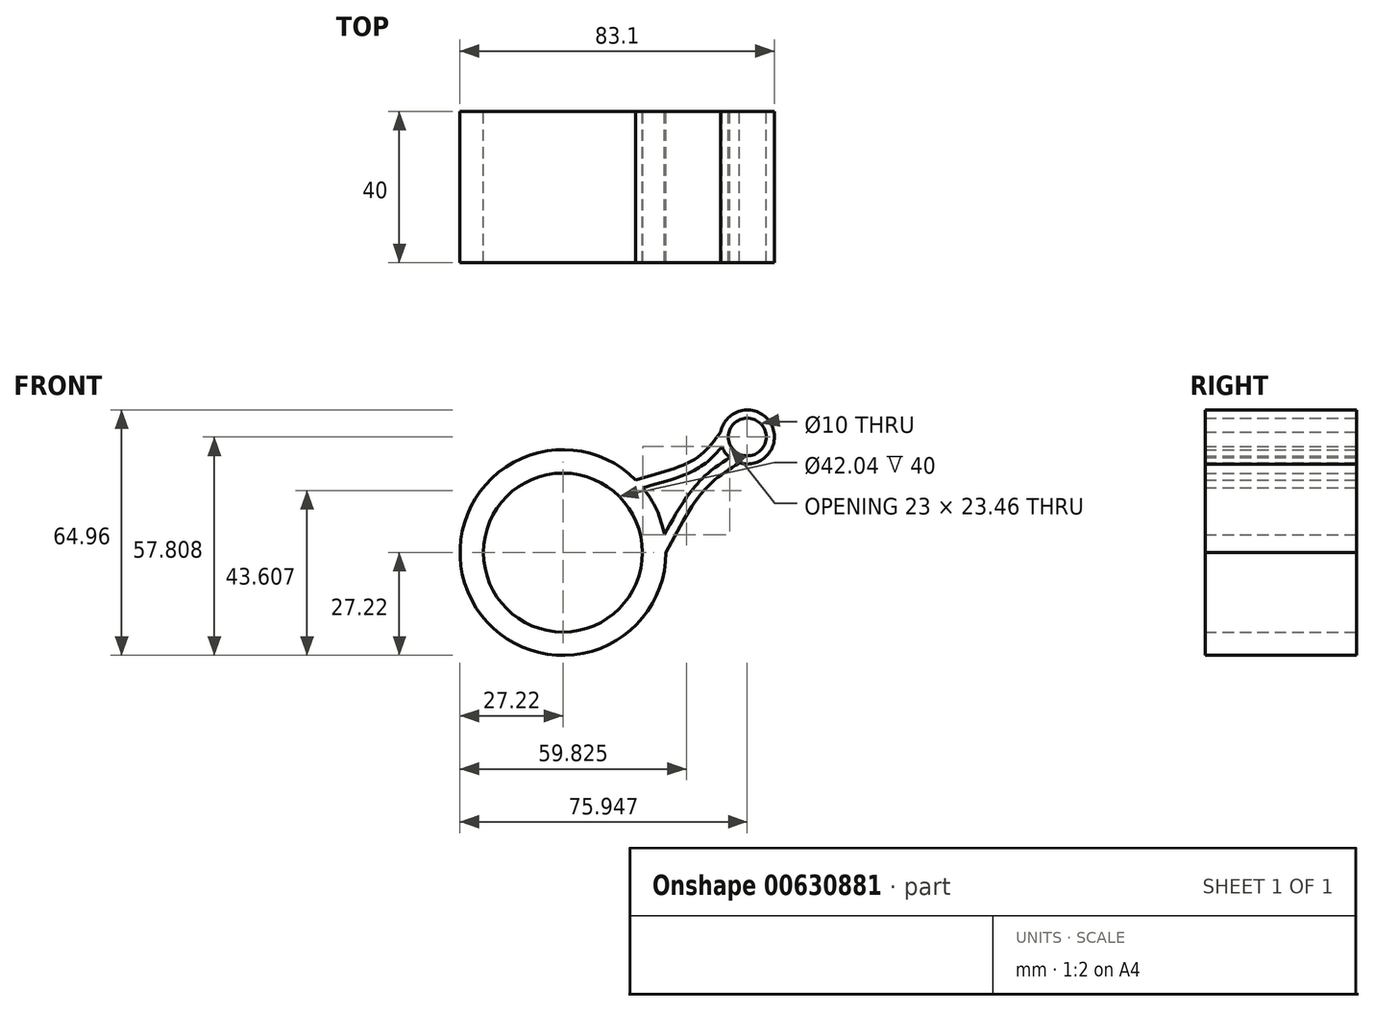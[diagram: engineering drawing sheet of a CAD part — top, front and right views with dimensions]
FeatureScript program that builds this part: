
annotation { "Feature Type Name" : "Feature", "Feature Type Description" : "" }
export const myFeature = defineFeature(function(context is Context, id is Id, definition is map)
    precondition{}
    {
        {
            var Q0;
            Q0=qCreatedBy(makeId("Front.planeOp"),FACE);
            var sketch = newSketch(context, id + "F0", { "sketchPlane" : qUnion([Q0])});
            skCircle(sketch, "E0", {"center": v(0, 0) * mm, "radius": 27.22 * mm});
            skLineSegment(sketch, "E1", {"start": v(0, 0) * mm, "end": v(0, 27.22) * mm});
            skLineSegment(sketch, "E2", {"start": v(0, 27.22) * mm, "end": v(0, 0) * mm});
            skLineSegment(sketch, "E3", {"start": v(27.22, 0) * mm, "end": v(0, 0) * mm});
            skLineSegment(sketch, "E4", {"start": v(0, 0) * mm, "end": v(19.24, 19.24) * mm});
            skCircle(sketch, "E5", {"center": v(0, 0) * mm, "radius": 21.02 * mm});
            skFitSpline(sketch, "E6", {"points": [v(27.22, 0) * mm, v(37.3, 16.46) * mm, v(46.6, 23.76) * mm], "startDerivative": vector(17.1, 32.9) * mm, "endDerivative": vector(21.89, 13.84) * mm});
            skFitSpline(sketch, "E7", {"points": [v(19.24, 19.24) * mm, v(34.77, 24.69) * mm, v(41.76, 31.96) * mm], "startDerivative": vector(29, 8.4) * mm, "endDerivative": vector(14.79, 19.6) * mm});
            skCircle(sketch, "E8", {"center": v(48.73, 30.59) * mm, "radius": 7.15 * mm});
            skCircle(sketch, "E9", {"center": v(48.73, 30.59) * mm, "radius": 5 * mm});
            skFitSpline(sketch, "E10.0", {"points": [v(19.94, 16.84) * mm, v(21.13, 17.19) * mm, v(23.6, 17.87) * mm, v(27.42, 18.96) * mm, v(30.52, 19.97) * mm, v(32.88, 20.9) * mm, v(34.28, 21.56) * mm, v(35.35, 22.12) * mm, v(36.13, 22.58) * mm, v(36.87, 23.06) * mm, v(37.8, 23.73) * mm, v(38.85, 24.61) * mm, v(40.36, 26.1) * mm, v(41.97, 28.05) * mm, v(43.15, 29.65) * mm, v(43.75, 30.45) * mm]});
            skFitSpline(sketch, "E11.0", {"points": [v(25, 1.15) * mm, v(25.7, 2.52) * mm, v(27.14, 5.28) * mm, v(29.35, 9.33) * mm, v(31.27, 12.52) * mm, v(32.88, 14.91) * mm, v(33.93, 16.32) * mm, v(34.8, 17.4) * mm, v(35.7, 18.42) * mm, v(36.84, 19.62) * mm, v(38.24, 20.9) * mm, v(40.13, 22.45) * mm, v(42.5, 24.12) * mm, v(44.36, 25.3) * mm, v(45.27, 25.87) * mm]});
            skSolve(sketch);
        }
        {
            var Q0;
            Q0 = qSketchRegion(id + "F0", true);
            extrude(context, id + "F1", {"entities" : qUnion([Q0]), "depth" : 40 * mm, "offsetDistance" : 25 * mm});
        }
    });
